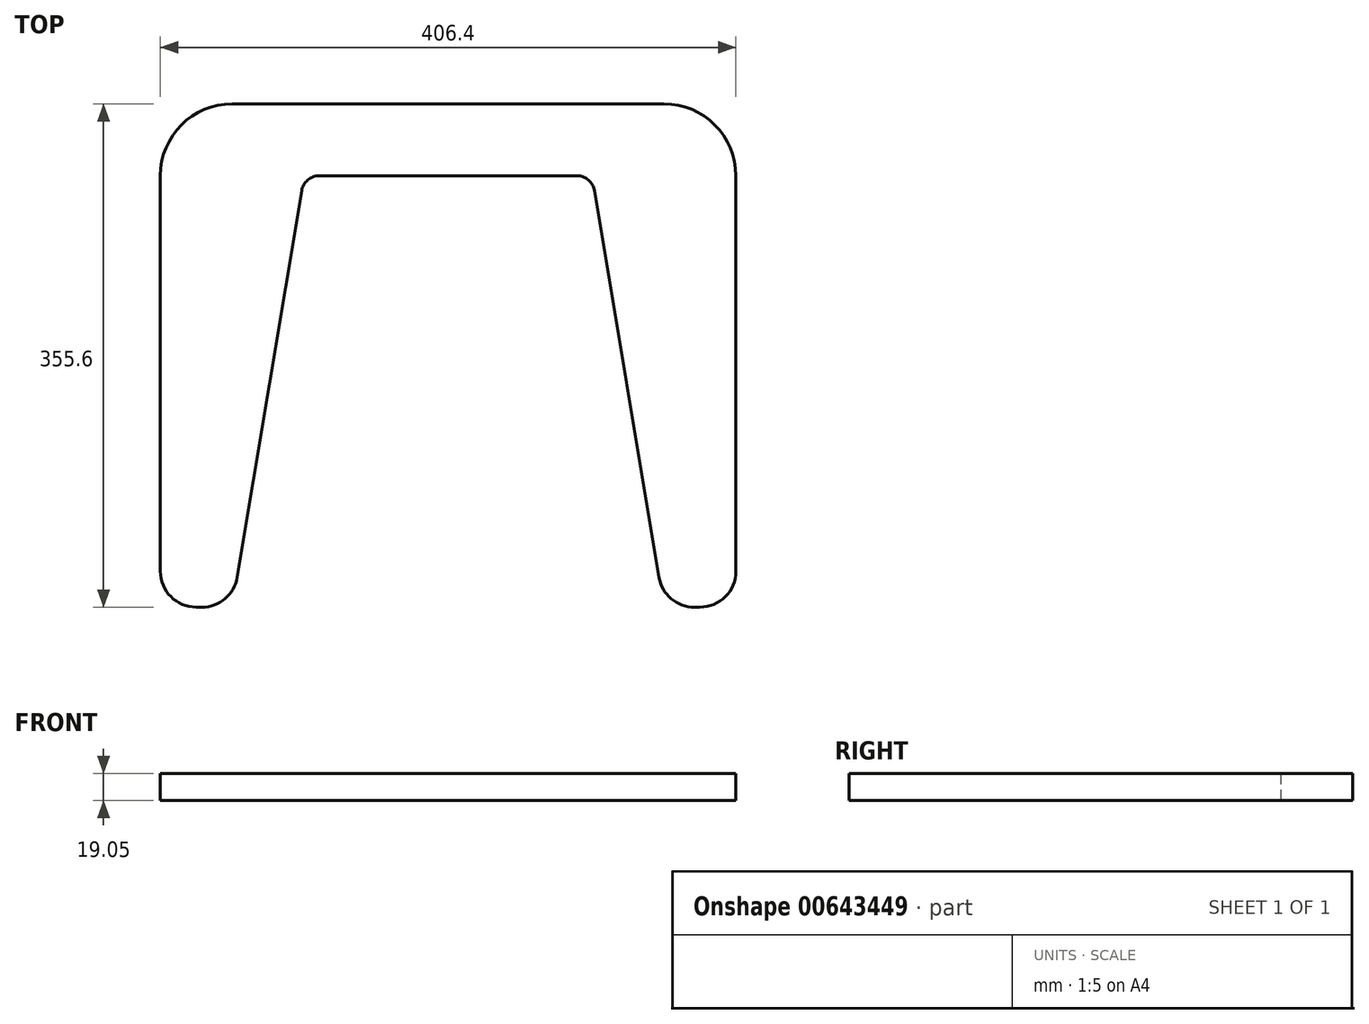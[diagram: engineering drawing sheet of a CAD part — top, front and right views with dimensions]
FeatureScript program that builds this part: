
annotation { "Feature Type Name" : "Feature", "Feature Type Description" : "" }
export const myFeature = defineFeature(function(context is Context, id is Id, definition is map)
    precondition{}
    {
        {
            var Q0;
            Q0=qCreatedBy(makeId("Top.planeOp"),FACE);
            var sketch = newSketch(context, id + "F0", { "sketchPlane" : qUnion([Q0])});
            skLineSegment(sketch, "E0", {"start": v(0, 0) * mm, "end": v(203.2, 0) * mm});
            skLineSegment(sketch, "E1", {"start": v(0, 0) * mm, "end": v(-101.6, 0) * mm});
            skLineSegment(sketch, "E2", {"start": v(101.6, 0) * mm, "end": v(101.6, 21.69) * mm, "construction": true});
            skLineSegment(sketch, "E3.MirrorCS", {"start": v(203.2, 0) * mm, "end": v(304.8, 0) * mm});
            skLineSegment(sketch, "E4", {"start": v(-101.6, 0) * mm, "end": v(-101.6, -355.6) * mm});
            skLineSegment(sketch, "E5.MirrorCS", {"start": v(304.8, 0) * mm, "end": v(304.8, -355.6) * mm});
            skLineSegment(sketch, "E6", {"start": v(-101.6, -355.6) * mm, "end": v(-50.8, -355.6) * mm});
            skLineSegment(sketch, "E7", {"start": v(0, 0) * mm, "end": v(0, -50.8) * mm, "construction": true});
            skLineSegment(sketch, "E8.MirrorCS", {"start": v(203.2, 0) * mm, "end": v(203.2, -50.8) * mm, "construction": true});
            skLineSegment(sketch, "E9", {"start": v(0, -50.8) * mm, "end": v(203.2, -50.8) * mm});
            skLineSegment(sketch, "E10.MirrorCS", {"start": v(304.8, -355.6) * mm, "end": v(254, -355.6) * mm});
            skLineSegment(sketch, "E11", {"start": v(-50.8, -355.6) * mm, "end": v(0, -50.8) * mm});
            skLineSegment(sketch, "E12", {"start": v(203.2, -50.8) * mm, "end": v(254, -355.6) * mm});
            skSolve(sketch);
        }
        {
            var Q0;
            Q0=makeQuery(id+"F0.imprint","IMPRINT",FACE,{"disambiguationData":[TD([[makeQuery(id+"F0.imprint","IMPRINT",EDGE,{"derivedFrom":sQuery(id+"F0.wireOp",EDGE,"E0")}),-1.0]])]});
            extrude(context, id + "F1", {"entities" : qUnion([Q0]), "depth" : 19.05 * mm, "offsetDistance" : 25.4 * mm});
        }
        {
            var Q0;
            Q0=makeQuery(id+"F1.opExtrude","SWEPT_EDGE",EDGE,{"disambiguationData":[OSD([sQuery(id+"F0.wireOp",EDGE,"E1"),sQuery(id+"F0.wireOp",EDGE,"E4")])]});
            var Q1;
            Q1=makeQuery(id+"F1.opExtrude","SWEPT_EDGE",EDGE,{"disambiguationData":[OSD([sQuery(id+"F0.wireOp",EDGE,"E3.MirrorCS"),sQuery(id+"F0.wireOp",EDGE,"E5.MirrorCS")])]});
            fillet(context, id + "F2", {"entities" : qUnion([Q0, Q1]), "radius" : 50.8 * mm, "tangentPropagation" : true, "allowEdgeOverflow" : false});
        }
        {
            var Q0;
            Q0=makeQuery(id+"F1.opExtrude","SWEPT_EDGE",EDGE,{"disambiguationData":[OSD([sQuery(id+"F0.wireOp",EDGE,"E4"),sQuery(id+"F0.wireOp",EDGE,"E6")])]});
            var Q1;
            Q1=makeQuery(id+"F1.opExtrude","SWEPT_EDGE",EDGE,{"disambiguationData":[OSD([sQuery(id+"F0.wireOp",EDGE,"E6"),sQuery(id+"F0.wireOp",EDGE,"E11")])]});
            var Q2;
            Q2=makeQuery(id+"F1.opExtrude","SWEPT_EDGE",EDGE,{"disambiguationData":[OSD([sQuery(id+"F0.wireOp",EDGE,"E5.MirrorCS"),sQuery(id+"F0.wireOp",EDGE,"E10.MirrorCS")])]});
            var Q3;
            Q3=makeQuery(id+"F1.opExtrude","SWEPT_EDGE",EDGE,{"disambiguationData":[OSD([sQuery(id+"F0.wireOp",EDGE,"E10.MirrorCS"),sQuery(id+"F0.wireOp",EDGE,"E12")])]});
            fillet(context, id + "F3", {"entities" : qUnion([Q0, Q1, Q2, Q3]), "radius" : 25.4 * mm, "tangentPropagation" : true, "allowEdgeOverflow" : false});
        }
        {
            var Q0;
            Q0=makeQuery(id+"F1.opExtrude","SWEPT_EDGE",EDGE,{"disambiguationData":[OSD([sQuery(id+"F0.wireOp",EDGE,"E9"),sQuery(id+"F0.wireOp",EDGE,"E12")])]});
            var Q1;
            Q1=makeQuery(id+"F1.opExtrude","SWEPT_EDGE",EDGE,{"disambiguationData":[OSD([sQuery(id+"F0.wireOp",EDGE,"E9"),sQuery(id+"F0.wireOp",EDGE,"E11")])]});
            fillet(context, id + "F4", {"entities" : qUnion([Q0, Q1]), "radius" : 12.7 * mm, "tangentPropagation" : true, "allowEdgeOverflow" : false});
        }
    });
